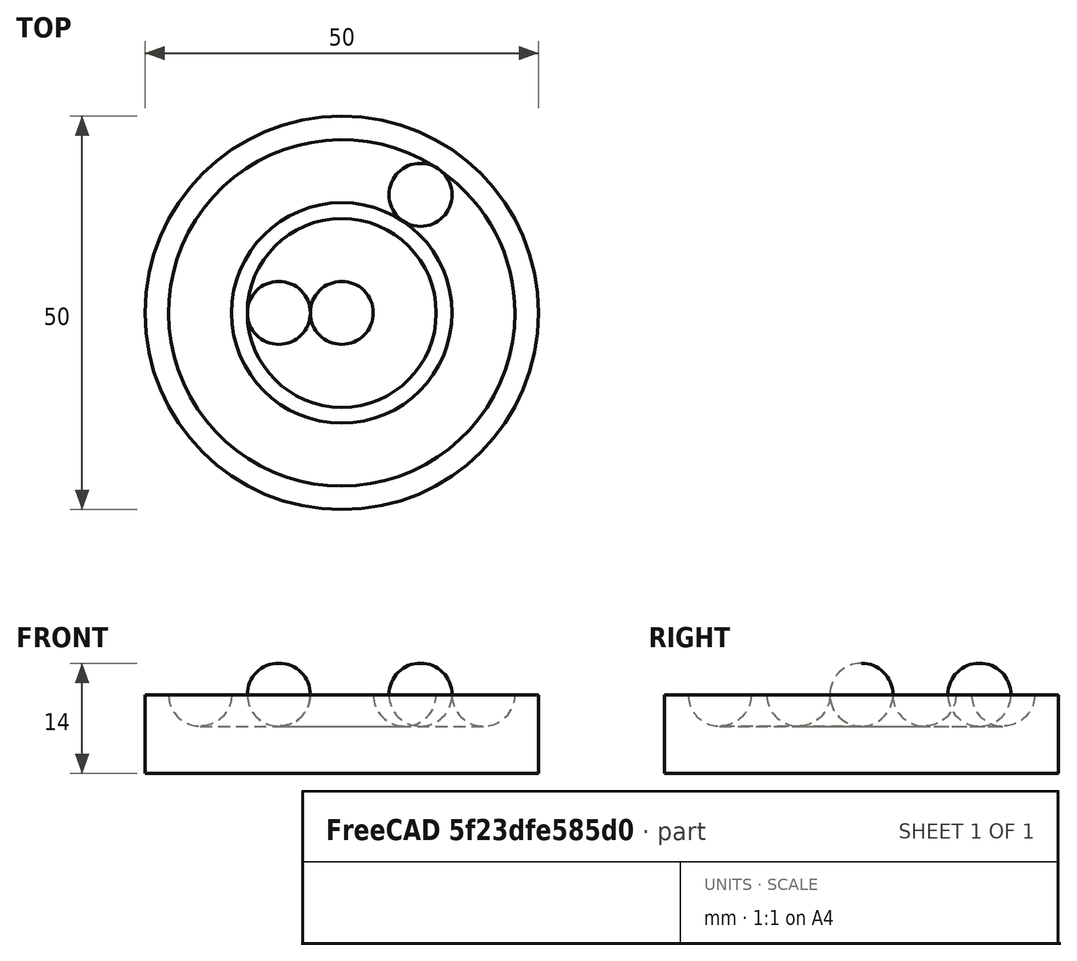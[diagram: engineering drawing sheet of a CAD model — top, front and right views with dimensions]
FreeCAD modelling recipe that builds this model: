
FCSTD DOCUMENT  (FreeCAD 0.18.4R)
Label: tutorial_freecad_ex15_c
License: All rights reserved
LicenseURL: http://en.wikipedia.org/wiki/All_rights_reserved
objects: Part::Torus×2, Part::Sphere×2, Part::Cylinder×1, Part::MultiFuse×1, Part::Cut×1
note: 7 computed .brp shape members not serialized (recipe doc carries the construction recipe); baked Part::Feature solids carry a one-line shape summary decoded from their .brp

FEATURE [Part::Cylinder] Cylinder  label="base"
  Angle = 360
  AttacherType = Attacher::AttachEngine3D
  Height = 10
  Radius = 25
FEATURE [Part::Torus] Torus  label="rail_interno"
  Angle1 = -180
  Angle2 = 180
  Angle3 = 360
  AttacherType = Attacher::AttachEngine3D
  Radius1 = 8
  Radius2 = 4
FEATURE [Part::Torus] Torus001  label="rail_externo"
  Angle1 = -180
  Angle2 = 180
  Angle3 = 360
  AttacherType = Attacher::AttachEngine3D
  Radius1 = 18
  Radius2 = 4
FEATURE [Part::MultiFuse] Fusion  label="railes"
  Placement = pos=(0,0,10) rot=(0,0,1;0rad)
  Refine = true
  Shapes = -> [Torus,Torus001]
FEATURE [Part::Cut] Cut  label="porta_railes"
  Base = -> Cylinder
  Refine = true
  Tool = -> Fusion
FEATURE [Part::Sphere] Sphere  label="boliche_01"
  Angle1 = -90
  Angle2 = 90
  Angle3 = 360
  AttacherType = Attacher::AttachEngine3D
  Placement = pos=(-8,0,10) rot=(0,0,1;0rad)
  Radius = 4
FEATURE [Part::Sphere] Sphere001  label="boliche_02"
  Angle1 = -90
  Angle2 = 90
  Angle3 = 360
  AttacherType = Attacher::AttachEngine3D
  Placement = pos=(10,15,10) rot=(0,0,1;0rad)
  Radius = 4
